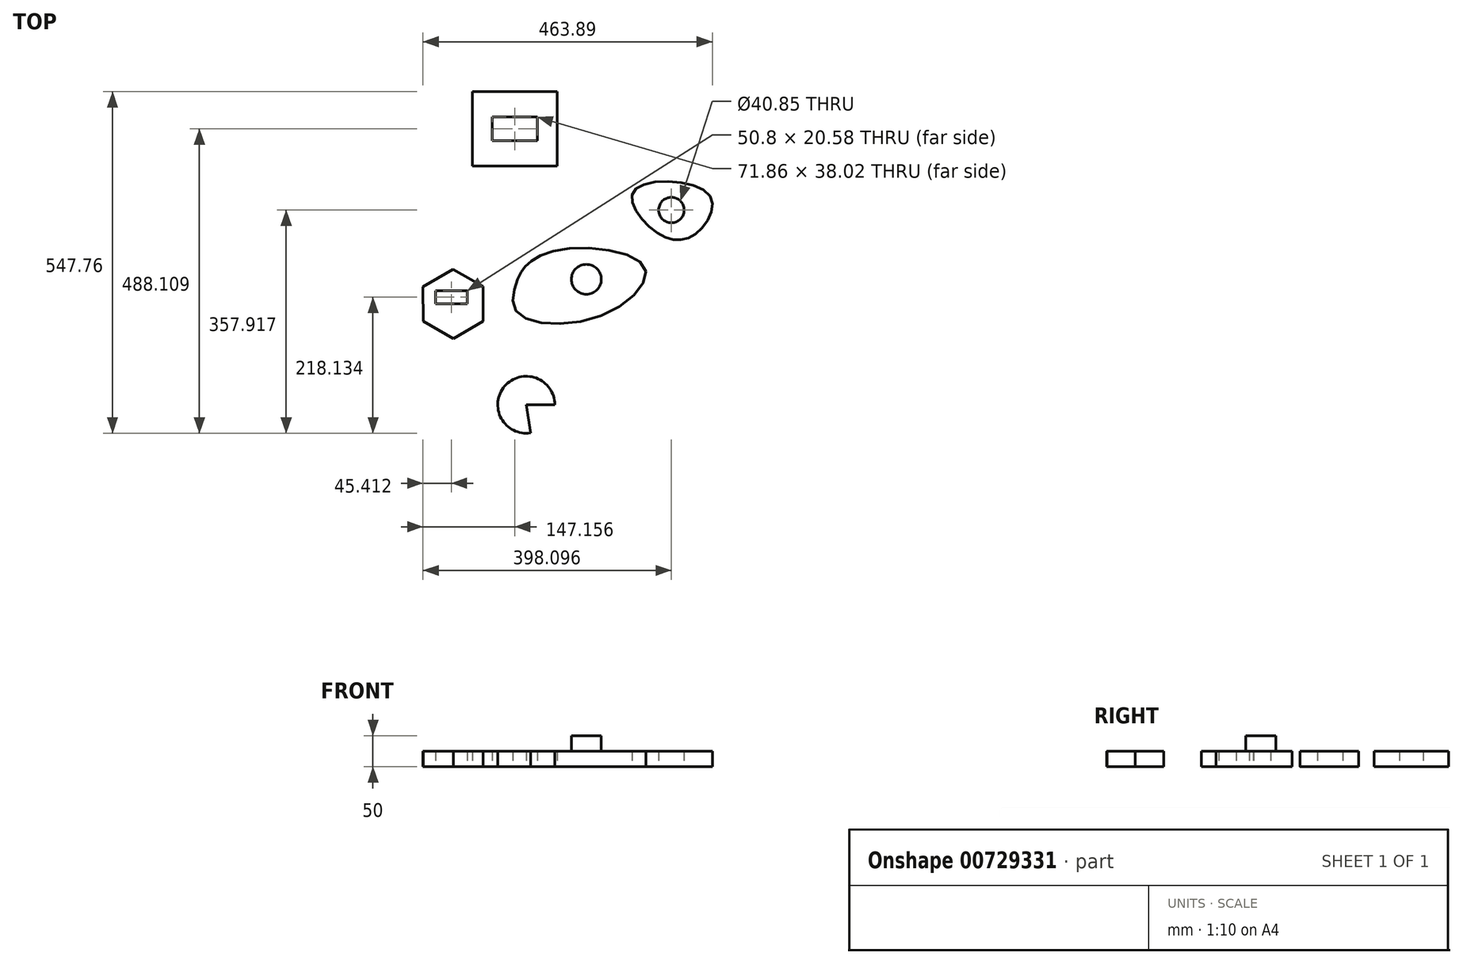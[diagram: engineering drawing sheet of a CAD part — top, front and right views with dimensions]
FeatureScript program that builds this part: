
annotation { "Feature Type Name" : "Feature", "Feature Type Description" : "" }
export const myFeature = defineFeature(function(context is Context, id is Id, definition is map)
    precondition{}
    {
        {
            var Q0;
            Q0=qCreatedBy(makeId("Top.planeOp"),FACE);
            var sketch = newSketch(context, id + "F0", { "sketchPlane" : qUnion([Q0])});
            skFitSpline(sketch, "E0", {"points": [v(-110.25, 7.33) * mm, v(-96.07, 29.82) * mm, v(-37.4, 55.74) * mm, v(93.14, 27.38) * mm, v(27.13, -49.38) * mm, v(-111.72, -44) * mm, v(-110.25, 7.33) * mm]});
            skSolve(sketch);
        }
        {
            var Q0;
            Q0=makeQuery(id+"F0.imprint","IMPRINT",FACE,{"disambiguationData":[TD([[makeQuery(id+"F0.imprint","IMPRINT",EDGE,{"derivedFrom":sQuery(id+"F0.wireOp",EDGE,"E0")}),-1.0]])]});
            extrude(context, id + "F1", {"entities" : qUnion([Q0]), "depth" : 25 * mm, "offsetDistance" : 25 * mm});
        }
        {
            var Q0;
            Q0=makeQuery(id+"F1.opExtrude","CAP_FACE",FACE,{"disambiguationData":[OSD([sQuery(id+"F0.wireOp",EDGE,"E0")])],"isStart":false});
            var sketch = newSketch(context, id + "F2", { "sketchPlane" : qUnion([Q0])});
            skCircle(sketch, "E1", {"center": v(0, 7.48) * mm, "radius": 23.97 * mm});
            skSolve(sketch);
        }
        {
            var Q0;
            Q0=makeQuery(id+"F2.imprint","IMPRINT",FACE,{"disambiguationData":[TD([[makeQuery(id+"F2.imprint","IMPRINT",EDGE,{"derivedFrom":sQuery(id+"F2.wireOp",EDGE,"E1")}),1.0]])]});
            extrude(context, id + "F3", {"entities" : qUnion([Q0]), "operationType" : NewBodyOperationType.ADD, "depth" : 25 * mm, "offsetDistance" : 25 * mm});
        }
        {
            var Q0;
            Q0=qCreatedBy(makeId("Top.planeOp"),FACE);
            var sketch = newSketch(context, id + "F4", { "sketchPlane" : qUnion([Q0])});
            skArc(sketch, "E2", {"start": v(-50.55, -193.63) * mm, "mid": v(-130.85, -163.82) * mm, "end": v(-89.46, -238.8) * mm});
            skLineSegment(sketch, "E3", {"start": v(-89.46, -238.8) * mm, "end": v(-96.23, -193.63) * mm});
            skLineSegment(sketch, "E4", {"start": v(-50.55, -193.63) * mm, "end": v(-96.23, -193.63) * mm});
            skSolve(sketch);
        }
        {
            var Q0;
            Q0=makeQuery(id+"F4.imprint","IMPRINT",FACE,{"disambiguationData":[TD([[makeQuery(id+"F4.imprint","IMPRINT",EDGE,{"derivedFrom":sQuery(id+"F4.wireOp",EDGE,"E2")}),1.0]])]});
            extrude(context, id + "F5", {"entities" : qUnion([Q0]), "depth" : 25 * mm, "offsetDistance" : 25 * mm});
        }
        {
            var Q0;
            Q0=qCreatedBy(makeId("Top.planeOp"),FACE);
            var sketch = newSketch(context, id + "F6", { "sketchPlane" : qUnion([Q0])});
            skFitSpline(sketch, "E5", {"points": [v(174.8, 80.15) * mm, v(112.78, 82.69) * mm, v(77.13, 150.06) * mm, v(195.93, 143.86) * mm, v(174.8, 80.15) * mm]});
            skCircle(sketch, "E6", {"center": v(136.34, 118.6) * mm, "radius": 20.43 * mm});
            skSolve(sketch);
        }
        {
            var Q0;
            Q0 = qSketchRegion(id + "F6", true);
            extrude(context, id + "F7", {"entities" : qUnion([Q0]), "depth" : 25 * mm, "offsetDistance" : 25 * mm});
        }
        {
            var Q0;
            Q0=qCreatedBy(makeId("Top.planeOp"),FACE);
            var sketch = newSketch(context, id + "F8", { "sketchPlane" : qUnion([Q0])});
            skCircle(sketch, "E7.cCircle", {"center": v(-213.45, -32) * mm, "radius": 48.22 * mm, "construction": true});
            skLineSegment(sketch, "E7.0", {"start": v(-261.76, -4.32) * mm, "end": v(-213.62, 23.68) * mm});
            skLineSegment(sketch, "E7.1", {"start": v(-213.62, 23.68) * mm, "end": v(-165.3, -4.02) * mm});
            skLineSegment(sketch, "E7.2", {"start": v(-165.3, -4.02) * mm, "end": v(-165.13, -59.7) * mm});
            skLineSegment(sketch, "E7.3", {"start": v(-165.13, -59.7) * mm, "end": v(-213.27, -87.7) * mm});
            skLineSegment(sketch, "E7.4", {"start": v(-213.27, -87.7) * mm, "end": v(-261.58, -60) * mm});
            skLineSegment(sketch, "E7.5", {"start": v(-261.58, -60) * mm, "end": v(-261.76, -4.32) * mm});
            skPoint(sketch, "E7.0.midPoint", {"position": v(-237.69, 9.68) * mm});
            skLineSegment(sketch, "E8.bottom", {"start": v(-241.75, -31.46) * mm, "end": v(-190.95, -31.46) * mm});
            skLineSegment(sketch, "E8.top", {"start": v(-241.75, -10.89) * mm, "end": v(-190.95, -10.89) * mm});
            skLineSegment(sketch, "E8.left", {"start": v(-241.75, -31.46) * mm, "end": v(-241.75, -10.89) * mm});
            skLineSegment(sketch, "E8.right", {"start": v(-190.95, -31.46) * mm, "end": v(-190.95, -10.89) * mm});
            skSolve(sketch);
        }
        {
            var Q0;
            Q0=makeQuery(id+"F8.imprint","IMPRINT",FACE,{"disambiguationData":[TD([[makeQuery(id+"F8.imprint","IMPRINT",EDGE,{"derivedFrom":sQuery(id+"F8.wireOp",EDGE,"E7.0")}),-1.0]])]});
            extrude(context, id + "F9", {"entities" : qUnion([Q0]), "depth" : 25 * mm, "offsetDistance" : 25 * mm});
        }
        {
            var Q0;
            Q0=qCreatedBy(makeId("Top.planeOp"),FACE);
            var sketch = newSketch(context, id + "F10", { "sketchPlane" : qUnion([Q0])});
            skLineSegment(sketch, "E9.bottom", {"start": v(-182.46, 189.15) * mm, "end": v(-46.75, 189.15) * mm});
            skLineSegment(sketch, "E9.top", {"start": v(-182.46, 308.45) * mm, "end": v(-46.75, 308.45) * mm});
            skLineSegment(sketch, "E9.left", {"start": v(-182.46, 189.15) * mm, "end": v(-182.46, 308.45) * mm});
            skLineSegment(sketch, "E9.right", {"start": v(-46.75, 189.15) * mm, "end": v(-46.75, 308.45) * mm});
            skPoint(sketch, "E9.middle", {"position": v(-114.6, 248.8) * mm});
            skLineSegment(sketch, "E10.bottom", {"start": v(-150.53, 229.79) * mm, "end": v(-78.67, 229.79) * mm});
            skLineSegment(sketch, "E10.top", {"start": v(-150.53, 267.8) * mm, "end": v(-78.67, 267.8) * mm});
            skLineSegment(sketch, "E10.left", {"start": v(-150.53, 229.79) * mm, "end": v(-150.53, 267.8) * mm});
            skLineSegment(sketch, "E10.right", {"start": v(-78.67, 229.79) * mm, "end": v(-78.67, 267.8) * mm});
            skSolve(sketch);
        }
        {
            var Q0;
            Q0=makeQuery(id+"F10.imprint","IMPRINT",FACE,{"disambiguationData":[TD([[makeQuery(id+"F10.imprint","IMPRINT",EDGE,{"derivedFrom":sQuery(id+"F10.wireOp",EDGE,"E9.bottom")}),1.0]])]});
            extrude(context, id + "F11", {"entities" : qUnion([Q0]), "depth" : 25 * mm, "offsetDistance" : 25 * mm});
        }
    });
